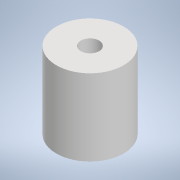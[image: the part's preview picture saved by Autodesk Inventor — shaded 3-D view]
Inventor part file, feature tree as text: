
AUTODESK INVENTOR PART (.ipt)
format: ipt  version: 2022 (Build 260153000, 153)  size: 93,184 bytes
history: native  units: mm
features: extrude x1, sketch x1
ambient origin geometry x8: Origin, YZ Plane, XZ Plane, XY Plane, X Axis, Y Axis, Z Axis, Center Point
bodies: Solid1 (feature_tree)
feature tree (2):
  extrude  "Extrusion1"  Depth=25.0mm
  sketch  "Sketch1"  dims[d0=6.0mm d1=22.0mm d2=25.0mm d3=0.0mm]
